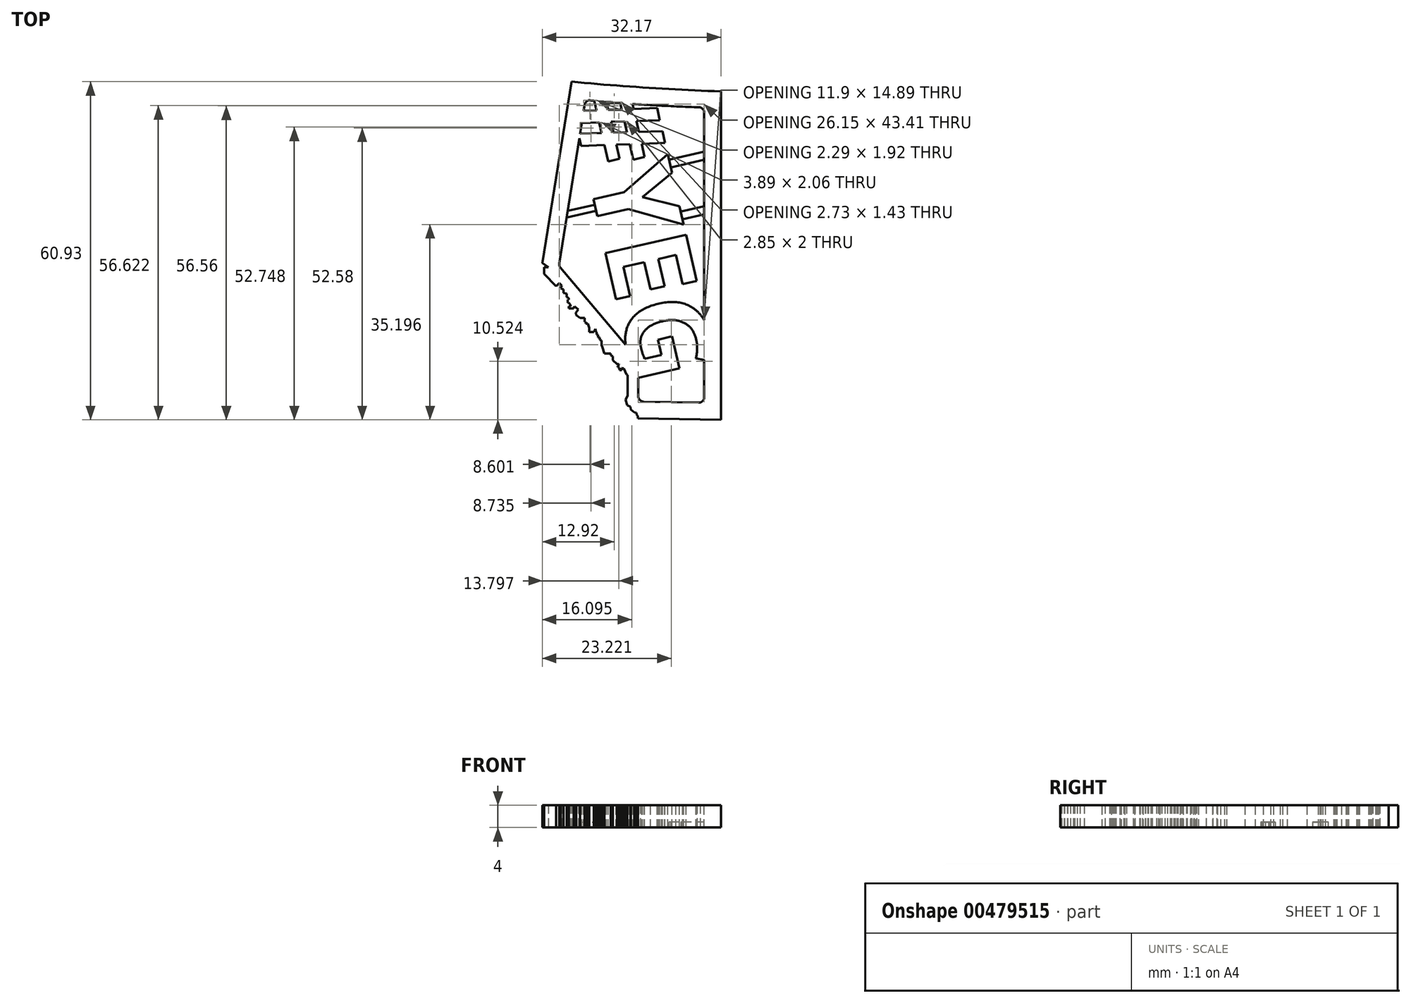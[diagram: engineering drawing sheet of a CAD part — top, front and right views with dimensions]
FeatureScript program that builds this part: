
annotation { "Feature Type Name" : "Feature", "Feature Type Description" : "" }
export const myFeature = defineFeature(function(context is Context, id is Id, definition is map)
    precondition{}
    {
        {
            var Q0;
            Q0=qCreatedBy(makeId("Top.planeOp"),FACE);
            var sketch = newSketch(context, id + "F0", { "sketchPlane" : qUnion([Q0])});
            skLineSegment(sketch, "E0", {"start": v(12.94, 76.8) * mm, "end": v(7.68, 44.1) * mm});
            skLineSegment(sketch, "E1", {"start": v(7.68, 44.1) * mm, "end": v(8.75, 43.35) * mm});
            skLineSegment(sketch, "E2", {"start": v(8.75, 43.35) * mm, "end": v(7.97, 43.35) * mm});
            skLineSegment(sketch, "E3", {"start": v(7.97, 43.35) * mm, "end": v(7.97, 42.17) * mm});
            skLineSegment(sketch, "E4", {"start": v(7.97, 42.17) * mm, "end": v(10.17, 39.93) * mm});
            skLineSegment(sketch, "E5", {"start": v(10.17, 39.93) * mm, "end": v(10.74, 40.49) * mm});
            skLineSegment(sketch, "E6", {"start": v(10.74, 40.49) * mm, "end": v(11.19, 40.03) * mm});
            skLineSegment(sketch, "E7", {"start": v(11.19, 40.03) * mm, "end": v(11, 39.57) * mm});
            skLineSegment(sketch, "E8", {"start": v(11, 39.57) * mm, "end": v(11.46, 39.39) * mm});
            skLineSegment(sketch, "E9", {"start": v(11.46, 39.39) * mm, "end": v(11.46, 38.73) * mm});
            skLineSegment(sketch, "E10", {"start": v(11.46, 38.73) * mm, "end": v(12.08, 38.61) * mm});
            skLineSegment(sketch, "E11", {"start": v(12.08, 38.61) * mm, "end": v(12.08, 37.96) * mm});
            skLineSegment(sketch, "E12", {"start": v(12.08, 37.96) * mm, "end": v(12.25, 37.87) * mm});
            skLineSegment(sketch, "E13", {"start": v(12.25, 37.87) * mm, "end": v(12.46, 37.8) * mm});
            skLineSegment(sketch, "E14", {"start": v(12.46, 37.8) * mm, "end": v(12.46, 37.52) * mm});
            skLineSegment(sketch, "E15", {"start": v(12.46, 37.52) * mm, "end": v(12.25, 37.52) * mm});
            skLineSegment(sketch, "E16", {"start": v(12.25, 37.52) * mm, "end": v(12.25, 36.96) * mm});
            skLineSegment(sketch, "E17", {"start": v(12.25, 36.96) * mm, "end": v(12.43, 36.93) * mm});
            skLineSegment(sketch, "E18", {"start": v(12.43, 36.93) * mm, "end": v(12.75, 36.55) * mm});
            skLineSegment(sketch, "E19", {"start": v(12.75, 36.55) * mm, "end": v(12.75, 36.3) * mm});
            skLineSegment(sketch, "E20", {"start": v(12.75, 36.3) * mm, "end": v(12.46, 36.3) * mm});
            skLineSegment(sketch, "E21", {"start": v(12.46, 36.3) * mm, "end": v(12.46, 35.94) * mm});
            skLineSegment(sketch, "E22", {"start": v(12.46, 35.94) * mm, "end": v(13.34, 35.94) * mm});
            skLineSegment(sketch, "E23", {"start": v(13.34, 35.94) * mm, "end": v(13.45, 36.34) * mm});
            skLineSegment(sketch, "E24", {"start": v(13.45, 36.34) * mm, "end": v(14.19, 35.72) * mm});
            skLineSegment(sketch, "E25", {"start": v(14.19, 35.72) * mm, "end": v(13.73, 35.19) * mm});
            skLineSegment(sketch, "E26", {"start": v(13.73, 35.19) * mm, "end": v(13.79, 34.75) * mm});
            skLineSegment(sketch, "E27", {"start": v(13.79, 34.75) * mm, "end": v(14.47, 34.2) * mm});
            skLineSegment(sketch, "E28", {"start": v(14.47, 34.2) * mm, "end": v(15.28, 34.2) * mm});
            skLineSegment(sketch, "E29", {"start": v(15.28, 34.2) * mm, "end": v(15.28, 33.54) * mm});
            skLineSegment(sketch, "E30", {"start": v(15.28, 33.54) * mm, "end": v(15.46, 33.54) * mm});
            skLineSegment(sketch, "E31", {"start": v(15.46, 33.54) * mm, "end": v(15.46, 33.22) * mm});
            skLineSegment(sketch, "E32", {"start": v(15.46, 33.22) * mm, "end": v(15.87, 33.22) * mm});
            skLineSegment(sketch, "E33", {"start": v(15.87, 33.22) * mm, "end": v(16.14, 32.43) * mm});
            skLineSegment(sketch, "E34", {"start": v(16.14, 32.43) * mm, "end": v(16.14, 31.7) * mm});
            skLineSegment(sketch, "E35", {"start": v(16.14, 31.7) * mm, "end": v(16.97, 31.7) * mm});
            skLineSegment(sketch, "E36", {"start": v(16.97, 31.7) * mm, "end": v(17.27, 32.23) * mm});
            skLineSegment(sketch, "E37", {"start": v(17.27, 32.23) * mm, "end": v(17.33, 31.74) * mm});
            skLineSegment(sketch, "E38", {"start": v(17.33, 31.74) * mm, "end": v(17.48, 31.65) * mm});
            skLineSegment(sketch, "E39", {"start": v(17.48, 31.65) * mm, "end": v(17.48, 31.25) * mm});
            skLineSegment(sketch, "E40", {"start": v(17.48, 31.25) * mm, "end": v(17.7, 31.18) * mm});
            skLineSegment(sketch, "E41", {"start": v(17.7, 31.18) * mm, "end": v(17.7, 30.7) * mm});
            skLineSegment(sketch, "E42", {"start": v(17.7, 30.7) * mm, "end": v(18.01, 30.66) * mm});
            skLineSegment(sketch, "E43", {"start": v(18.01, 30.66) * mm, "end": v(18.01, 30.29) * mm});
            skLineSegment(sketch, "E44", {"start": v(18.01, 30.29) * mm, "end": v(18.18, 30.2) * mm});
            skLineSegment(sketch, "E45", {"start": v(18.18, 30.2) * mm, "end": v(18.33, 30.17) * mm});
            skLineSegment(sketch, "E46", {"start": v(18.33, 30.17) * mm, "end": v(18.33, 29.33) * mm});
            skLineSegment(sketch, "E47", {"start": v(18.33, 29.33) * mm, "end": v(18.46, 29) * mm});
            skLineSegment(sketch, "E48", {"start": v(18.46, 29) * mm, "end": v(18.83, 27.8) * mm});
            skLineSegment(sketch, "E49", {"start": v(18.83, 27.8) * mm, "end": v(20, 27.8) * mm});
            skLineSegment(sketch, "E50", {"start": v(20, 27.8) * mm, "end": v(20, 27.5) * mm});
            skLineSegment(sketch, "E51", {"start": v(20, 27.5) * mm, "end": v(20.36, 27.3) * mm});
            skLineSegment(sketch, "E52", {"start": v(20.36, 27.3) * mm, "end": v(20.36, 26.6) * mm});
            skLineSegment(sketch, "E53", {"start": v(20.36, 26.6) * mm, "end": v(21.15, 25.9) * mm});
            skLineSegment(sketch, "E54", {"start": v(21.15, 25.9) * mm, "end": v(21.45, 25.9) * mm});
            skLineSegment(sketch, "E55", {"start": v(21.45, 25.9) * mm, "end": v(21.5, 25.75) * mm});
            skLineSegment(sketch, "E56", {"start": v(21.5, 25.75) * mm, "end": v(21.21, 25.6) * mm});
            skLineSegment(sketch, "E57", {"start": v(21.21, 25.6) * mm, "end": v(21.3, 25.31) * mm});
            skLineSegment(sketch, "E58", {"start": v(21.3, 25.31) * mm, "end": v(21.54, 25.28) * mm});
            skLineSegment(sketch, "E59", {"start": v(21.54, 25.28) * mm, "end": v(21.6, 24.78) * mm});
            skLineSegment(sketch, "E60", {"start": v(21.6, 24.78) * mm, "end": v(21.94, 24.82) * mm});
            skLineSegment(sketch, "E61", {"start": v(21.94, 24.82) * mm, "end": v(21.99, 25.2) * mm});
            skLineSegment(sketch, "E62", {"start": v(21.99, 25.2) * mm, "end": v(22.33, 25.1) * mm});
            skLineSegment(sketch, "E63", {"start": v(22.33, 25.1) * mm, "end": v(22.84, 23.96) * mm});
            skLineSegment(sketch, "E64", {"start": v(22.84, 23.96) * mm, "end": v(23.05, 23.94) * mm});
            skLineSegment(sketch, "E65", {"start": v(23.05, 23.94) * mm, "end": v(23.05, 22.88) * mm});
            skLineSegment(sketch, "E66", {"start": v(23.05, 22.88) * mm, "end": v(23.05, 20.17) * mm});
            skLineSegment(sketch, "E67", {"start": v(23.05, 20.17) * mm, "end": v(22.65, 19.46) * mm});
            skLineSegment(sketch, "E68", {"start": v(22.65, 19.46) * mm, "end": v(22.95, 18.48) * mm});
            skLineSegment(sketch, "E69", {"start": v(22.95, 18.48) * mm, "end": v(23.56, 18.23) * mm});
            skLineSegment(sketch, "E70", {"start": v(23.56, 18.23) * mm, "end": v(23.64, 17.74) * mm});
            skLineSegment(sketch, "E71", {"start": v(23.64, 17.74) * mm, "end": v(24.27, 17.22) * mm});
            skLineSegment(sketch, "E72", {"start": v(24.27, 17.22) * mm, "end": v(24.63, 17.14) * mm});
            skLineSegment(sketch, "E73", {"start": v(24.63, 17.14) * mm, "end": v(24.72, 16.67) * mm});
            skLineSegment(sketch, "E74", {"start": v(24.72, 16.67) * mm, "end": v(24.9, 16.57) * mm});
            skLineSegment(sketch, "E75", {"start": v(24.9, 16.57) * mm, "end": v(24.9, 16.14) * mm});
            skLineSegment(sketch, "E76", {"start": v(24.9, 16.14) * mm, "end": v(39.85, 15.87) * mm});
            skLineSegment(sketch, "E77", {"start": v(39.85, 15.87) * mm, "end": v(39.85, 75.04) * mm});
            skFitSpline(sketch, "E78", {"points": [v(12.94, 76.8) * mm, v(39.85, 75.04) * mm], "startDerivative": vector(26.48, -2.57) * mm, "endDerivative": vector(26.93, -1.05) * mm});
            skLineSegment(sketch, "E79.0", {"start": v(15.31, 72.63) * mm, "end": v(10.71, 44.07) * mm});
            skFitSpline(sketch, "E80.0", {"points": [v(12.65, 73.81) * mm, v(21.55, 72.95) * mm, v(30.71, 72.4) * mm, v(39.73, 72.04) * mm]});
            skLineSegment(sketch, "E81.0", {"start": v(25.93, 19.12) * mm, "end": v(35.83, 18.95) * mm});
            skLineSegment(sketch, "E82.trimOffspring", {"start": v(36.85, 19.95) * mm, "end": v(36.85, 71.2) * mm});
            skLineSegment(sketch, "E83", {"start": v(24.95, 20.12) * mm, "end": v(24.95, 26.3) * mm});
            skLineSegment(sketch, "E84", {"start": v(24.72, 26.95) * mm, "end": v(10.93, 43.26) * mm});
            skPoint(sketch, "E85.visualSharp", {"position": v(15.46, 73.55) * mm});
            skArc(sketch, "E85.filletArc", {"start": v(16.38, 73.47) * mm, "mid": v(15.68, 73.26) * mm, "end": v(15.31, 72.63) * mm});
            skPoint(sketch, "E86.visualSharp", {"position": v(36.85, 72.16) * mm});
            skArc(sketch, "E86.filletArc", {"start": v(36.85, 71.2) * mm, "mid": v(36.57, 71.9) * mm, "end": v(35.9, 72.2) * mm});
            skPoint(sketch, "E87.visualSharp", {"position": v(36.85, 18.93) * mm});
            skArc(sketch, "E87.filletArc", {"start": v(35.83, 18.95) * mm, "mid": v(36.55, 19.23) * mm, "end": v(36.85, 19.95) * mm});
            skPoint(sketch, "E88.visualSharp", {"position": v(24.95, 19.14) * mm});
            skArc(sketch, "E88.filletArc", {"start": v(24.95, 20.12) * mm, "mid": v(25.24, 19.42) * mm, "end": v(25.93, 19.12) * mm});
            skPoint(sketch, "E89.visualSharp", {"position": v(24.95, 26.67) * mm});
            skArc(sketch, "E89.filletArc", {"start": v(24.95, 26.3) * mm, "mid": v(24.9, 26.64) * mm, "end": v(24.72, 26.95) * mm});
            skPoint(sketch, "E90.visualSharp", {"position": v(10.64, 43.62) * mm});
            skArc(sketch, "E90.filletArc", {"start": v(10.71, 44.07) * mm, "mid": v(10.73, 43.64) * mm, "end": v(10.93, 43.26) * mm});
            skSolve(sketch);
        }
        {
            var Q0;
            Q0=makeQuery(id+"F0.imprint","IMPRINT",FACE,{"disambiguationData":[TD([[makeQuery(id+"F0.imprint","IMPRINT",EDGE,{"derivedFrom":sQuery(id+"F0.wireOp",EDGE,"E0")}),1.0]])]});
            extrude(context, id + "F1", {"entities" : qUnion([Q0]), "depth" : 4 * mm});
        }
        {
            var Q0;
            Q0=makeQuery(id+"F1.opExtrude","CAP_FACE",FACE,{"disambiguationData":[OSD([sQuery(id+"F0.wireOp",EDGE,"E0"),sQuery(id+"F0.wireOp",EDGE,"E1"),sQuery(id+"F0.wireOp",EDGE,"E2"),sQuery(id+"F0.wireOp",EDGE,"E3"),sQuery(id+"F0.wireOp",EDGE,"E4"),sQuery(id+"F0.wireOp",EDGE,"E5"),sQuery(id+"F0.wireOp",EDGE,"E6"),sQuery(id+"F0.wireOp",EDGE,"E7"),sQuery(id+"F0.wireOp",EDGE,"E8"),sQuery(id+"F0.wireOp",EDGE,"E9"),sQuery(id+"F0.wireOp",EDGE,"E10"),sQuery(id+"F0.wireOp",EDGE,"E11"),sQuery(id+"F0.wireOp",EDGE,"E12"),sQuery(id+"F0.wireOp",EDGE,"E13"),sQuery(id+"F0.wireOp",EDGE,"E14"),sQuery(id+"F0.wireOp",EDGE,"E15"),sQuery(id+"F0.wireOp",EDGE,"E16"),sQuery(id+"F0.wireOp",EDGE,"E17"),sQuery(id+"F0.wireOp",EDGE,"E18"),sQuery(id+"F0.wireOp",EDGE,"E19"),sQuery(id+"F0.wireOp",EDGE,"E20"),sQuery(id+"F0.wireOp",EDGE,"E21"),sQuery(id+"F0.wireOp",EDGE,"E22"),sQuery(id+"F0.wireOp",EDGE,"E23"),sQuery(id+"F0.wireOp",EDGE,"E24"),sQuery(id+"F0.wireOp",EDGE,"E25"),sQuery(id+"F0.wireOp",EDGE,"E26"),sQuery(id+"F0.wireOp",EDGE,"E27"),sQuery(id+"F0.wireOp",EDGE,"E28"),sQuery(id+"F0.wireOp",EDGE,"E29"),sQuery(id+"F0.wireOp",EDGE,"E30"),sQuery(id+"F0.wireOp",EDGE,"E31"),sQuery(id+"F0.wireOp",EDGE,"E32"),sQuery(id+"F0.wireOp",EDGE,"E33"),sQuery(id+"F0.wireOp",EDGE,"E34"),sQuery(id+"F0.wireOp",EDGE,"E35"),sQuery(id+"F0.wireOp",EDGE,"E36"),sQuery(id+"F0.wireOp",EDGE,"E37"),sQuery(id+"F0.wireOp",EDGE,"E38"),sQuery(id+"F0.wireOp",EDGE,"E39"),sQuery(id+"F0.wireOp",EDGE,"E40"),sQuery(id+"F0.wireOp",EDGE,"E41"),sQuery(id+"F0.wireOp",EDGE,"E42"),sQuery(id+"F0.wireOp",EDGE,"E43"),sQuery(id+"F0.wireOp",EDGE,"E44"),sQuery(id+"F0.wireOp",EDGE,"E45"),sQuery(id+"F0.wireOp",EDGE,"E46"),sQuery(id+"F0.wireOp",EDGE,"E47"),sQuery(id+"F0.wireOp",EDGE,"E48"),sQuery(id+"F0.wireOp",EDGE,"E49"),sQuery(id+"F0.wireOp",EDGE,"E50"),sQuery(id+"F0.wireOp",EDGE,"E51"),sQuery(id+"F0.wireOp",EDGE,"E52"),sQuery(id+"F0.wireOp",EDGE,"E53"),sQuery(id+"F0.wireOp",EDGE,"E54"),sQuery(id+"F0.wireOp",EDGE,"E55"),sQuery(id+"F0.wireOp",EDGE,"E56"),sQuery(id+"F0.wireOp",EDGE,"E57"),sQuery(id+"F0.wireOp",EDGE,"E58"),sQuery(id+"F0.wireOp",EDGE,"E59"),sQuery(id+"F0.wireOp",EDGE,"E60"),sQuery(id+"F0.wireOp",EDGE,"E61"),sQuery(id+"F0.wireOp",EDGE,"E62"),sQuery(id+"F0.wireOp",EDGE,"E63"),sQuery(id+"F0.wireOp",EDGE,"E64"),sQuery(id+"F0.wireOp",EDGE,"E65"),sQuery(id+"F0.wireOp",EDGE,"E66"),sQuery(id+"F0.wireOp",EDGE,"E67"),sQuery(id+"F0.wireOp",EDGE,"E68"),sQuery(id+"F0.wireOp",EDGE,"E69"),sQuery(id+"F0.wireOp",EDGE,"E70"),sQuery(id+"F0.wireOp",EDGE,"E71"),sQuery(id+"F0.wireOp",EDGE,"E72"),sQuery(id+"F0.wireOp",EDGE,"E73"),sQuery(id+"F0.wireOp",EDGE,"E74"),sQuery(id+"F0.wireOp",EDGE,"E75"),sQuery(id+"F0.wireOp",EDGE,"E76"),sQuery(id+"F0.wireOp",EDGE,"E77"),sQuery(id+"F0.wireOp",EDGE,"E78"),sQuery(id+"F0.wireOp",EDGE,"E79.0"),sQuery(id+"F0.wireOp",EDGE,"E80.0"),sQuery(id+"F0.wireOp",EDGE,"E81.0"),sQuery(id+"F0.wireOp",EDGE,"E82.trimOffspring"),sQuery(id+"F0.wireOp",EDGE,"E83"),sQuery(id+"F0.wireOp",EDGE,"E84"),sQuery(id+"F0.wireOp",EDGE,"E85.filletArc"),sQuery(id+"F0.wireOp",EDGE,"E86.filletArc"),sQuery(id+"F0.wireOp",EDGE,"E87.filletArc"),sQuery(id+"F0.wireOp",EDGE,"E88.filletArc"),sQuery(id+"F0.wireOp",EDGE,"E89.filletArc"),sQuery(id+"F0.wireOp",EDGE,"E90.filletArc")])],"isStart":false});
            var sketch = newSketch(context, id + "F2", { "sketchPlane" : qUnion([Q0])});
            skText(sketch, "E91", { "text": "#YEG", "fontName": "NotoSans-Bold.ttf"});
            const initialGuessF2  = {"E91": [0.01276, 0.07352, 0.22255, -0.97492, 0.015]};
            skSetInitialGuess(sketch, initialGuessF2);
            skSolve(sketch);
        }
        {
            var Q0;
            Q0=makeQuery(id+"F2.imprint","IMPRINT",FACE,{"disambiguationData":[TD([[makeQuery(id+"F2.imprint","IMPRINT",EDGE,{"derivedFrom":sQuery(id+"F2.wireOp",EDGE,"E91.sketch_text.stroke-0")}),-1.0]])]});
            var Q1;
            Q1=makeQuery(id+"F2.imprint","IMPRINT",FACE,{"disambiguationData":[TD([[makeQuery(id+"F2.imprint","IMPRINT",EDGE,{"derivedFrom":sQuery(id+"F2.wireOp",EDGE,"E91.sketch_text.stroke-32")}),-1.0]])]});
            var Q2;
            Q2=makeQuery(id+"F2.imprint","IMPRINT",FACE,{"disambiguationData":[TD([[makeQuery(id+"F2.imprint","IMPRINT",EDGE,{"derivedFrom":sQuery(id+"F2.wireOp",EDGE,"E91.sketch_text.stroke-41")}),-1.0]])]});
            var Q3;
            Q3=makeQuery(id+"F2.imprint","IMPRINT",FACE,{"disambiguationData":[TD([[makeQuery(id+"F2.imprint","IMPRINT",EDGE,{"derivedFrom":sQuery(id+"F2.wireOp",EDGE,"E91.sketch_text.stroke-53")}),-1.0]])]});
            var Q4;
            Q4=makeQuery(id+"F1.opExtrude","CAP_FACE",FACE,{"disambiguationData":[OSD([sQuery(id+"F0.wireOp",EDGE,"E0"),sQuery(id+"F0.wireOp",EDGE,"E1"),sQuery(id+"F0.wireOp",EDGE,"E2"),sQuery(id+"F0.wireOp",EDGE,"E3"),sQuery(id+"F0.wireOp",EDGE,"E4"),sQuery(id+"F0.wireOp",EDGE,"E5"),sQuery(id+"F0.wireOp",EDGE,"E6"),sQuery(id+"F0.wireOp",EDGE,"E7"),sQuery(id+"F0.wireOp",EDGE,"E8"),sQuery(id+"F0.wireOp",EDGE,"E9"),sQuery(id+"F0.wireOp",EDGE,"E10"),sQuery(id+"F0.wireOp",EDGE,"E11"),sQuery(id+"F0.wireOp",EDGE,"E12"),sQuery(id+"F0.wireOp",EDGE,"E13"),sQuery(id+"F0.wireOp",EDGE,"E14"),sQuery(id+"F0.wireOp",EDGE,"E15"),sQuery(id+"F0.wireOp",EDGE,"E16"),sQuery(id+"F0.wireOp",EDGE,"E17"),sQuery(id+"F0.wireOp",EDGE,"E18"),sQuery(id+"F0.wireOp",EDGE,"E19"),sQuery(id+"F0.wireOp",EDGE,"E20"),sQuery(id+"F0.wireOp",EDGE,"E21"),sQuery(id+"F0.wireOp",EDGE,"E22"),sQuery(id+"F0.wireOp",EDGE,"E23"),sQuery(id+"F0.wireOp",EDGE,"E24"),sQuery(id+"F0.wireOp",EDGE,"E25"),sQuery(id+"F0.wireOp",EDGE,"E26"),sQuery(id+"F0.wireOp",EDGE,"E27"),sQuery(id+"F0.wireOp",EDGE,"E28"),sQuery(id+"F0.wireOp",EDGE,"E29"),sQuery(id+"F0.wireOp",EDGE,"E30"),sQuery(id+"F0.wireOp",EDGE,"E31"),sQuery(id+"F0.wireOp",EDGE,"E32"),sQuery(id+"F0.wireOp",EDGE,"E33"),sQuery(id+"F0.wireOp",EDGE,"E34"),sQuery(id+"F0.wireOp",EDGE,"E35"),sQuery(id+"F0.wireOp",EDGE,"E36"),sQuery(id+"F0.wireOp",EDGE,"E37"),sQuery(id+"F0.wireOp",EDGE,"E38"),sQuery(id+"F0.wireOp",EDGE,"E39"),sQuery(id+"F0.wireOp",EDGE,"E40"),sQuery(id+"F0.wireOp",EDGE,"E41"),sQuery(id+"F0.wireOp",EDGE,"E42"),sQuery(id+"F0.wireOp",EDGE,"E43"),sQuery(id+"F0.wireOp",EDGE,"E44"),sQuery(id+"F0.wireOp",EDGE,"E45"),sQuery(id+"F0.wireOp",EDGE,"E46"),sQuery(id+"F0.wireOp",EDGE,"E47"),sQuery(id+"F0.wireOp",EDGE,"E48"),sQuery(id+"F0.wireOp",EDGE,"E49"),sQuery(id+"F0.wireOp",EDGE,"E50"),sQuery(id+"F0.wireOp",EDGE,"E51"),sQuery(id+"F0.wireOp",EDGE,"E52"),sQuery(id+"F0.wireOp",EDGE,"E53"),sQuery(id+"F0.wireOp",EDGE,"E54"),sQuery(id+"F0.wireOp",EDGE,"E55"),sQuery(id+"F0.wireOp",EDGE,"E56"),sQuery(id+"F0.wireOp",EDGE,"E57"),sQuery(id+"F0.wireOp",EDGE,"E58"),sQuery(id+"F0.wireOp",EDGE,"E59"),sQuery(id+"F0.wireOp",EDGE,"E60"),sQuery(id+"F0.wireOp",EDGE,"E61"),sQuery(id+"F0.wireOp",EDGE,"E62"),sQuery(id+"F0.wireOp",EDGE,"E63"),sQuery(id+"F0.wireOp",EDGE,"E64"),sQuery(id+"F0.wireOp",EDGE,"E65"),sQuery(id+"F0.wireOp",EDGE,"E66"),sQuery(id+"F0.wireOp",EDGE,"E67"),sQuery(id+"F0.wireOp",EDGE,"E68"),sQuery(id+"F0.wireOp",EDGE,"E69"),sQuery(id+"F0.wireOp",EDGE,"E70"),sQuery(id+"F0.wireOp",EDGE,"E71"),sQuery(id+"F0.wireOp",EDGE,"E72"),sQuery(id+"F0.wireOp",EDGE,"E73"),sQuery(id+"F0.wireOp",EDGE,"E74"),sQuery(id+"F0.wireOp",EDGE,"E75"),sQuery(id+"F0.wireOp",EDGE,"E76"),sQuery(id+"F0.wireOp",EDGE,"E77"),sQuery(id+"F0.wireOp",EDGE,"E78"),sQuery(id+"F0.wireOp",EDGE,"E79.0"),sQuery(id+"F0.wireOp",EDGE,"E80.0"),sQuery(id+"F0.wireOp",EDGE,"E81.0"),sQuery(id+"F0.wireOp",EDGE,"E82.trimOffspring"),sQuery(id+"F0.wireOp",EDGE,"E83"),sQuery(id+"F0.wireOp",EDGE,"E84"),sQuery(id+"F0.wireOp",EDGE,"E85.filletArc"),sQuery(id+"F0.wireOp",EDGE,"E86.filletArc"),sQuery(id+"F0.wireOp",EDGE,"E87.filletArc"),sQuery(id+"F0.wireOp",EDGE,"E88.filletArc"),sQuery(id+"F0.wireOp",EDGE,"E89.filletArc"),sQuery(id+"F0.wireOp",EDGE,"E90.filletArc")])],"isStart":true});
            extrude(context, id + "F3", {"entities" : qUnion([Q0, Q1, Q2, Q3]), "endBound" : BoundingType.UP_TO_SURFACE, "oppositeDirection" : true, "endBoundEntityFace" : qUnion([Q4]), "depth" : 25 * mm});
        }
        {
            var Q0;
            Q0=makeQuery(id+"F3.opExtrude","SWEPT_BODY",BODY,{"disambiguationData":[OSD([sQuery(id+"F0.wireOp",EDGE,"E79.0"),sQuery(id+"F0.wireOp",EDGE,"E80.0"),sQuery(id+"F2.wireOp",EDGE,"E91.sketch_text.stroke-0"),sQuery(id+"F2.wireOp",EDGE,"E91.sketch_text.stroke-1"),sQuery(id+"F2.wireOp",EDGE,"E91.sketch_text.stroke-2"),sQuery(id+"F2.wireOp",EDGE,"E91.sketch_text.stroke-3"),sQuery(id+"F2.wireOp",EDGE,"E91.sketch_text.stroke-4"),sQuery(id+"F2.wireOp",EDGE,"E91.sketch_text.stroke-5"),sQuery(id+"F2.wireOp",EDGE,"E91.sketch_text.stroke-6"),sQuery(id+"F2.wireOp",EDGE,"E91.sketch_text.stroke-7"),sQuery(id+"F2.wireOp",EDGE,"E91.sketch_text.stroke-8"),sQuery(id+"F2.wireOp",EDGE,"E91.sketch_text.stroke-10"),sQuery(id+"F2.wireOp",EDGE,"E91.sketch_text.stroke-11"),sQuery(id+"F2.wireOp",EDGE,"E91.sketch_text.stroke-13"),sQuery(id+"F2.wireOp",EDGE,"E91.sketch_text.stroke-14"),sQuery(id+"F2.wireOp",EDGE,"E91.sketch_text.stroke-15"),sQuery(id+"F2.wireOp",EDGE,"E91.sketch_text.stroke-17"),sQuery(id+"F2.wireOp",EDGE,"E91.sketch_text.stroke-18"),sQuery(id+"F2.wireOp",EDGE,"E91.sketch_text.stroke-19"),sQuery(id+"F2.wireOp",EDGE,"E91.sketch_text.stroke-20"),sQuery(id+"F2.wireOp",EDGE,"E91.sketch_text.stroke-21"),sQuery(id+"F2.wireOp",EDGE,"E91.sketch_text.stroke-22"),sQuery(id+"F2.wireOp",EDGE,"E91.sketch_text.stroke-23"),sQuery(id+"F2.wireOp",EDGE,"E91.sketch_text.stroke-24"),sQuery(id+"F2.wireOp",EDGE,"E91.sketch_text.stroke-25"),sQuery(id+"F2.wireOp",EDGE,"E91.sketch_text.stroke-26"),sQuery(id+"F2.wireOp",EDGE,"E91.sketch_text.stroke-27"),sQuery(id+"F2.wireOp",EDGE,"E91.sketch_text.stroke-28"),sQuery(id+"F2.wireOp",EDGE,"E91.sketch_text.stroke-29"),sQuery(id+"F2.wireOp",EDGE,"E91.sketch_text.stroke-30"),sQuery(id+"F2.wireOp",EDGE,"E91.sketch_text.stroke-31")])]});
            var Q1;
            Q1=makeQuery(id+"F1.opExtrude","SWEPT_BODY",BODY,{"disambiguationData":[OSD([sQuery(id+"F0.wireOp",EDGE,"E0"),sQuery(id+"F0.wireOp",EDGE,"E1"),sQuery(id+"F0.wireOp",EDGE,"E2"),sQuery(id+"F0.wireOp",EDGE,"E3"),sQuery(id+"F0.wireOp",EDGE,"E4"),sQuery(id+"F0.wireOp",EDGE,"E5"),sQuery(id+"F0.wireOp",EDGE,"E6"),sQuery(id+"F0.wireOp",EDGE,"E7"),sQuery(id+"F0.wireOp",EDGE,"E8"),sQuery(id+"F0.wireOp",EDGE,"E9"),sQuery(id+"F0.wireOp",EDGE,"E10"),sQuery(id+"F0.wireOp",EDGE,"E11"),sQuery(id+"F0.wireOp",EDGE,"E12"),sQuery(id+"F0.wireOp",EDGE,"E13"),sQuery(id+"F0.wireOp",EDGE,"E14"),sQuery(id+"F0.wireOp",EDGE,"E15"),sQuery(id+"F0.wireOp",EDGE,"E16"),sQuery(id+"F0.wireOp",EDGE,"E17"),sQuery(id+"F0.wireOp",EDGE,"E18"),sQuery(id+"F0.wireOp",EDGE,"E19"),sQuery(id+"F0.wireOp",EDGE,"E20"),sQuery(id+"F0.wireOp",EDGE,"E21"),sQuery(id+"F0.wireOp",EDGE,"E22"),sQuery(id+"F0.wireOp",EDGE,"E23"),sQuery(id+"F0.wireOp",EDGE,"E24"),sQuery(id+"F0.wireOp",EDGE,"E25"),sQuery(id+"F0.wireOp",EDGE,"E26"),sQuery(id+"F0.wireOp",EDGE,"E27"),sQuery(id+"F0.wireOp",EDGE,"E28"),sQuery(id+"F0.wireOp",EDGE,"E29"),sQuery(id+"F0.wireOp",EDGE,"E30"),sQuery(id+"F0.wireOp",EDGE,"E31"),sQuery(id+"F0.wireOp",EDGE,"E32"),sQuery(id+"F0.wireOp",EDGE,"E33"),sQuery(id+"F0.wireOp",EDGE,"E34"),sQuery(id+"F0.wireOp",EDGE,"E35"),sQuery(id+"F0.wireOp",EDGE,"E36"),sQuery(id+"F0.wireOp",EDGE,"E37"),sQuery(id+"F0.wireOp",EDGE,"E38"),sQuery(id+"F0.wireOp",EDGE,"E39"),sQuery(id+"F0.wireOp",EDGE,"E40"),sQuery(id+"F0.wireOp",EDGE,"E41"),sQuery(id+"F0.wireOp",EDGE,"E42"),sQuery(id+"F0.wireOp",EDGE,"E43"),sQuery(id+"F0.wireOp",EDGE,"E44"),sQuery(id+"F0.wireOp",EDGE,"E45"),sQuery(id+"F0.wireOp",EDGE,"E46"),sQuery(id+"F0.wireOp",EDGE,"E47"),sQuery(id+"F0.wireOp",EDGE,"E48"),sQuery(id+"F0.wireOp",EDGE,"E49"),sQuery(id+"F0.wireOp",EDGE,"E50"),sQuery(id+"F0.wireOp",EDGE,"E51"),sQuery(id+"F0.wireOp",EDGE,"E52"),sQuery(id+"F0.wireOp",EDGE,"E53"),sQuery(id+"F0.wireOp",EDGE,"E54"),sQuery(id+"F0.wireOp",EDGE,"E55"),sQuery(id+"F0.wireOp",EDGE,"E56"),sQuery(id+"F0.wireOp",EDGE,"E57"),sQuery(id+"F0.wireOp",EDGE,"E58"),sQuery(id+"F0.wireOp",EDGE,"E59"),sQuery(id+"F0.wireOp",EDGE,"E60"),sQuery(id+"F0.wireOp",EDGE,"E61"),sQuery(id+"F0.wireOp",EDGE,"E62"),sQuery(id+"F0.wireOp",EDGE,"E63"),sQuery(id+"F0.wireOp",EDGE,"E64"),sQuery(id+"F0.wireOp",EDGE,"E65"),sQuery(id+"F0.wireOp",EDGE,"E66"),sQuery(id+"F0.wireOp",EDGE,"E67"),sQuery(id+"F0.wireOp",EDGE,"E68"),sQuery(id+"F0.wireOp",EDGE,"E69"),sQuery(id+"F0.wireOp",EDGE,"E70"),sQuery(id+"F0.wireOp",EDGE,"E71"),sQuery(id+"F0.wireOp",EDGE,"E72"),sQuery(id+"F0.wireOp",EDGE,"E73"),sQuery(id+"F0.wireOp",EDGE,"E74"),sQuery(id+"F0.wireOp",EDGE,"E75"),sQuery(id+"F0.wireOp",EDGE,"E76"),sQuery(id+"F0.wireOp",EDGE,"E77"),sQuery(id+"F0.wireOp",EDGE,"E78"),sQuery(id+"F0.wireOp",EDGE,"E79.0"),sQuery(id+"F0.wireOp",EDGE,"E80.0"),sQuery(id+"F0.wireOp",EDGE,"E81.0"),sQuery(id+"F0.wireOp",EDGE,"E82.trimOffspring"),sQuery(id+"F0.wireOp",EDGE,"E83"),sQuery(id+"F0.wireOp",EDGE,"E84"),sQuery(id+"F0.wireOp",EDGE,"E85.filletArc"),sQuery(id+"F0.wireOp",EDGE,"E86.filletArc"),sQuery(id+"F0.wireOp",EDGE,"E87.filletArc"),sQuery(id+"F0.wireOp",EDGE,"E88.filletArc"),sQuery(id+"F0.wireOp",EDGE,"E89.filletArc"),sQuery(id+"F0.wireOp",EDGE,"E90.filletArc")])]});
            booleanBodies(context, id + "F4", {"operationType" : BooleanOperationType.UNION, "tools" : qUnion([Q0, Q1])});
        }
        {
            var Q0;
            Q0=makeQuery(id+"F3.opExtrude","SWEPT_BODY",BODY,{"disambiguationData":[OSD([sQuery(id+"F0.wireOp",EDGE,"E82.trimOffspring"),sQuery(id+"F0.wireOp",EDGE,"E83"),sQuery(id+"F0.wireOp",EDGE,"E84"),sQuery(id+"F0.wireOp",EDGE,"E89.filletArc"),sQuery(id+"F2.wireOp",EDGE,"E91.sketch_text.stroke-53"),sQuery(id+"F2.wireOp",EDGE,"E91.sketch_text.stroke-54"),sQuery(id+"F2.wireOp",EDGE,"E91.sketch_text.stroke-57"),sQuery(id+"F2.wireOp",EDGE,"E91.sketch_text.stroke-58"),sQuery(id+"F2.wireOp",EDGE,"E91.sketch_text.stroke-59"),sQuery(id+"F2.wireOp",EDGE,"E91.sketch_text.stroke-60"),sQuery(id+"F2.wireOp",EDGE,"E91.sketch_text.stroke-62"),sQuery(id+"F2.wireOp",EDGE,"E91.sketch_text.stroke-63"),sQuery(id+"F2.wireOp",EDGE,"E91.sketch_text.stroke-64"),sQuery(id+"F2.wireOp",EDGE,"E91.sketch_text.stroke-65"),sQuery(id+"F2.wireOp",EDGE,"E91.sketch_text.stroke-66"),sQuery(id+"F2.wireOp",EDGE,"E91.sketch_text.stroke-67"),sQuery(id+"F2.wireOp",EDGE,"E91.sketch_text.stroke-68"),sQuery(id+"F2.wireOp",EDGE,"E91.sketch_text.stroke-69"),sQuery(id+"F2.wireOp",EDGE,"E91.sketch_text.stroke-70"),sQuery(id+"F2.wireOp",EDGE,"E91.sketch_text.stroke-71")])]});
            var Q1;
            Q1=makeQuery(id+"F3.opExtrude","SWEPT_BODY",BODY,{"disambiguationData":[OSD([sQuery(id+"F0.wireOp",EDGE,"E79.0"),sQuery(id+"F0.wireOp",EDGE,"E80.0"),sQuery(id+"F2.wireOp",EDGE,"E91.sketch_text.stroke-0"),sQuery(id+"F2.wireOp",EDGE,"E91.sketch_text.stroke-1"),sQuery(id+"F2.wireOp",EDGE,"E91.sketch_text.stroke-2"),sQuery(id+"F2.wireOp",EDGE,"E91.sketch_text.stroke-3"),sQuery(id+"F2.wireOp",EDGE,"E91.sketch_text.stroke-4"),sQuery(id+"F2.wireOp",EDGE,"E91.sketch_text.stroke-5"),sQuery(id+"F2.wireOp",EDGE,"E91.sketch_text.stroke-6"),sQuery(id+"F2.wireOp",EDGE,"E91.sketch_text.stroke-7"),sQuery(id+"F2.wireOp",EDGE,"E91.sketch_text.stroke-8"),sQuery(id+"F2.wireOp",EDGE,"E91.sketch_text.stroke-10"),sQuery(id+"F2.wireOp",EDGE,"E91.sketch_text.stroke-11"),sQuery(id+"F2.wireOp",EDGE,"E91.sketch_text.stroke-13"),sQuery(id+"F2.wireOp",EDGE,"E91.sketch_text.stroke-14"),sQuery(id+"F2.wireOp",EDGE,"E91.sketch_text.stroke-15"),sQuery(id+"F2.wireOp",EDGE,"E91.sketch_text.stroke-17"),sQuery(id+"F2.wireOp",EDGE,"E91.sketch_text.stroke-18"),sQuery(id+"F2.wireOp",EDGE,"E91.sketch_text.stroke-19"),sQuery(id+"F2.wireOp",EDGE,"E91.sketch_text.stroke-20"),sQuery(id+"F2.wireOp",EDGE,"E91.sketch_text.stroke-21"),sQuery(id+"F2.wireOp",EDGE,"E91.sketch_text.stroke-22"),sQuery(id+"F2.wireOp",EDGE,"E91.sketch_text.stroke-23"),sQuery(id+"F2.wireOp",EDGE,"E91.sketch_text.stroke-24"),sQuery(id+"F2.wireOp",EDGE,"E91.sketch_text.stroke-25"),sQuery(id+"F2.wireOp",EDGE,"E91.sketch_text.stroke-26"),sQuery(id+"F2.wireOp",EDGE,"E91.sketch_text.stroke-27"),sQuery(id+"F2.wireOp",EDGE,"E91.sketch_text.stroke-28"),sQuery(id+"F2.wireOp",EDGE,"E91.sketch_text.stroke-29"),sQuery(id+"F2.wireOp",EDGE,"E91.sketch_text.stroke-30"),sQuery(id+"F2.wireOp",EDGE,"E91.sketch_text.stroke-31")])]});
            booleanBodies(context, id + "F5", {"operationType" : BooleanOperationType.UNION, "tools" : qUnion([Q0, Q1])});
        }
        {
            var Q0;
            Q0=makeQuery(id+"F3.opExtrude","SWEPT_FACE",FACE,{"disambiguationData":[OSD([sQuery(id+"F2.wireOp",EDGE,"E91.sketch_text.stroke-39")])]});
            var sketch = newSketch(context, id + "F6", { "sketchPlane" : qUnion([Q0])});
            skLineSegment(sketch, "E92.0.0", {"start": v(51.97, 4) * mm, "end": v(51.97, 0) * mm});
            skLineSegment(sketch, "E92.0.1", {"start": v(51.97, 0) * mm, "end": v(55.38, 0) * mm});
            skLineSegment(sketch, "E92.0.2", {"start": v(55.38, 0) * mm, "end": v(55.38, 4) * mm});
            skLineSegment(sketch, "E92.0.3", {"start": v(55.38, 4) * mm, "end": v(51.97, 4) * mm});
            skLineSegment(sketch, "E93.0", {"start": v(52.97, 3) * mm, "end": v(52.97, 1) * mm});
            skLineSegment(sketch, "E93.1", {"start": v(54.38, 3) * mm, "end": v(52.97, 3) * mm});
            skLineSegment(sketch, "E93.2", {"start": v(54.38, 1) * mm, "end": v(54.38, 3) * mm});
            skLineSegment(sketch, "E93.3", {"start": v(52.97, 1) * mm, "end": v(54.38, 1) * mm});
            skLineSegment(sketch, "E94", {"start": v(52.97, 1) * mm, "end": v(52.97, 0) * mm});
            skLineSegment(sketch, "E95", {"start": v(54.38, 1) * mm, "end": v(54.38, 0) * mm});
            skSolve(sketch);
        }
        {
            var Q0;
            Q0=makeQuery(id+"F6.imprint","IMPRINT",FACE,{"disambiguationData":[TD([[makeQuery(id+"F6.imprint","IMPRINT",EDGE,{"derivedFrom":sQuery(id+"F6.wireOp",EDGE,"E93.3")}),-1.0]])]});
            var Q1;
            {var subQ7=sQuery(id+"F0.wireOp",EDGE,"E86.filletArc");var subQ11=sQuery(id+"F0.wireOp",EDGE,"E82.trimOffspring");Q1=makeQuery(id+"F5.opBoolean","SPLIT",FACE,{"disambiguationData":[TD([makeQuery(id+"F1.opExtrude","SWEPT_FACE",FACE,{"disambiguationData":[OSD([subQ7])]})])],"derivedFrom":makeQuery(id+"F1.opExtrude","SWEPT_FACE",FACE,{"disambiguationData":[OSD([subQ11])]})});}
            extrude(context, id + "F7", {"entities" : qUnion([Q0]), "endBound" : BoundingType.UP_TO_SURFACE, "endBoundEntityFace" : qUnion([Q1]), "depth" : 25 * mm});
        }
        {
            var Q0;
            Q0=makeQuery(id+"F3.opExtrude","SWEPT_FACE",FACE,{"disambiguationData":[OSD([sQuery(id+"F2.wireOp",EDGE,"E91.sketch_text.stroke-33")])]});
            var sketch = newSketch(context, id + "F8", { "sketchPlane" : qUnion([Q0])});
            skLineSegment(sketch, "E96.0.0", {"start": v(42.38, 4) * mm, "end": v(42.38, 0) * mm});
            skLineSegment(sketch, "E96.0.1", {"start": v(42.38, 0) * mm, "end": v(45.78, 0) * mm});
            skLineSegment(sketch, "E96.0.2", {"start": v(45.78, 0) * mm, "end": v(45.78, 4) * mm});
            skLineSegment(sketch, "E96.0.3", {"start": v(45.78, 4) * mm, "end": v(42.38, 4) * mm});
            skLineSegment(sketch, "E97.0", {"start": v(43.38, 3) * mm, "end": v(43.38, 1) * mm});
            skLineSegment(sketch, "E97.1", {"start": v(44.78, 3) * mm, "end": v(43.38, 3) * mm});
            skLineSegment(sketch, "E97.2", {"start": v(44.78, 1) * mm, "end": v(44.78, 3) * mm});
            skLineSegment(sketch, "E97.3", {"start": v(43.38, 1) * mm, "end": v(44.78, 1) * mm});
            skLineSegment(sketch, "E98", {"start": v(43.38, 1) * mm, "end": v(43.38, 0) * mm});
            skLineSegment(sketch, "E99", {"start": v(44.78, 1) * mm, "end": v(44.78, 0) * mm});
            skSolve(sketch);
        }
        {
            var Q0;
            Q0=makeQuery(id+"F8.imprint","IMPRINT",FACE,{"disambiguationData":[TD([[makeQuery(id+"F8.imprint","IMPRINT",EDGE,{"derivedFrom":sQuery(id+"F8.wireOp",EDGE,"E97.3")}),-1.0]])]});
            var Q1;
            {var subQ7=sQuery(id+"F0.wireOp",EDGE,"E86.filletArc");var subQ11=sQuery(id+"F0.wireOp",EDGE,"E82.trimOffspring");Q1=makeQuery(id+"F5.opBoolean","SPLIT",FACE,{"disambiguationData":[TD([makeQuery(id+"F1.opExtrude","SWEPT_FACE",FACE,{"disambiguationData":[OSD([subQ7])]})])],"derivedFrom":makeQuery(id+"F1.opExtrude","SWEPT_FACE",FACE,{"disambiguationData":[OSD([subQ11])]})});}
            extrude(context, id + "F9", {"entities" : qUnion([Q0]), "endBound" : BoundingType.UP_TO_SURFACE, "endBoundEntityFace" : qUnion([Q1]), "depth" : 25 * mm});
        }
        {
            var Q0;
            Q0=makeQuery(id+"F3.opExtrude","SWEPT_FACE",FACE,{"disambiguationData":[OSD([sQuery(id+"F2.wireOp",EDGE,"E91.sketch_text.stroke-36")])]});
            var sketch = newSketch(context, id + "F10", { "sketchPlane" : qUnion([Q0])});
            skLineSegment(sketch, "E100.0.0", {"start": v(-50.45, 4) * mm, "end": v(-50.45, 0) * mm});
            skLineSegment(sketch, "E100.0.1", {"start": v(-50.45, 0) * mm, "end": v(-47.32, 0) * mm});
            skLineSegment(sketch, "E100.0.2", {"start": v(-47.32, 0) * mm, "end": v(-47.32, 4) * mm});
            skLineSegment(sketch, "E100.0.3", {"start": v(-47.32, 4) * mm, "end": v(-50.45, 4) * mm});
            skLineSegment(sketch, "E101.0", {"start": v(-49.45, 3) * mm, "end": v(-49.45, 1) * mm});
            skLineSegment(sketch, "E101.1", {"start": v(-48.32, 3) * mm, "end": v(-49.45, 3) * mm});
            skLineSegment(sketch, "E101.2", {"start": v(-48.32, 1) * mm, "end": v(-48.32, 3) * mm});
            skLineSegment(sketch, "E101.3", {"start": v(-49.45, 1) * mm, "end": v(-48.32, 1) * mm});
            skLineSegment(sketch, "E102", {"start": v(-49.45, 1) * mm, "end": v(-49.45, 0) * mm});
            skLineSegment(sketch, "E103", {"start": v(-48.32, 1) * mm, "end": v(-48.32, 0) * mm});
            skSolve(sketch);
        }
        {
            var Q0;
            Q0=makeQuery(id+"F10.imprint","IMPRINT",FACE,{"disambiguationData":[TD([[makeQuery(id+"F10.imprint","IMPRINT",EDGE,{"derivedFrom":sQuery(id+"F10.wireOp",EDGE,"E101.3")}),-1.0]])]});
            var Q1;
            {var subQ3=sQuery(id+"F0.wireOp",EDGE,"E79.0");var subQ4=sQuery(id+"F0.wireOp",EDGE,"E90.filletArc");Q1=makeQuery(id+"F4.opBoolean","SPLIT",FACE,{"disambiguationData":[TD([makeQuery(id+"F1.opExtrude","SWEPT_FACE",FACE,{"disambiguationData":[OSD([subQ4])]})])],"derivedFrom":makeQuery(id+"F1.opExtrude","SWEPT_FACE",FACE,{"disambiguationData":[OSD([subQ3])]})});}
            extrude(context, id + "F11", {"entities" : qUnion([Q0]), "endBound" : BoundingType.UP_TO_SURFACE, "endBoundEntityFace" : qUnion([Q1]), "depth" : 25 * mm});
        }
    });
